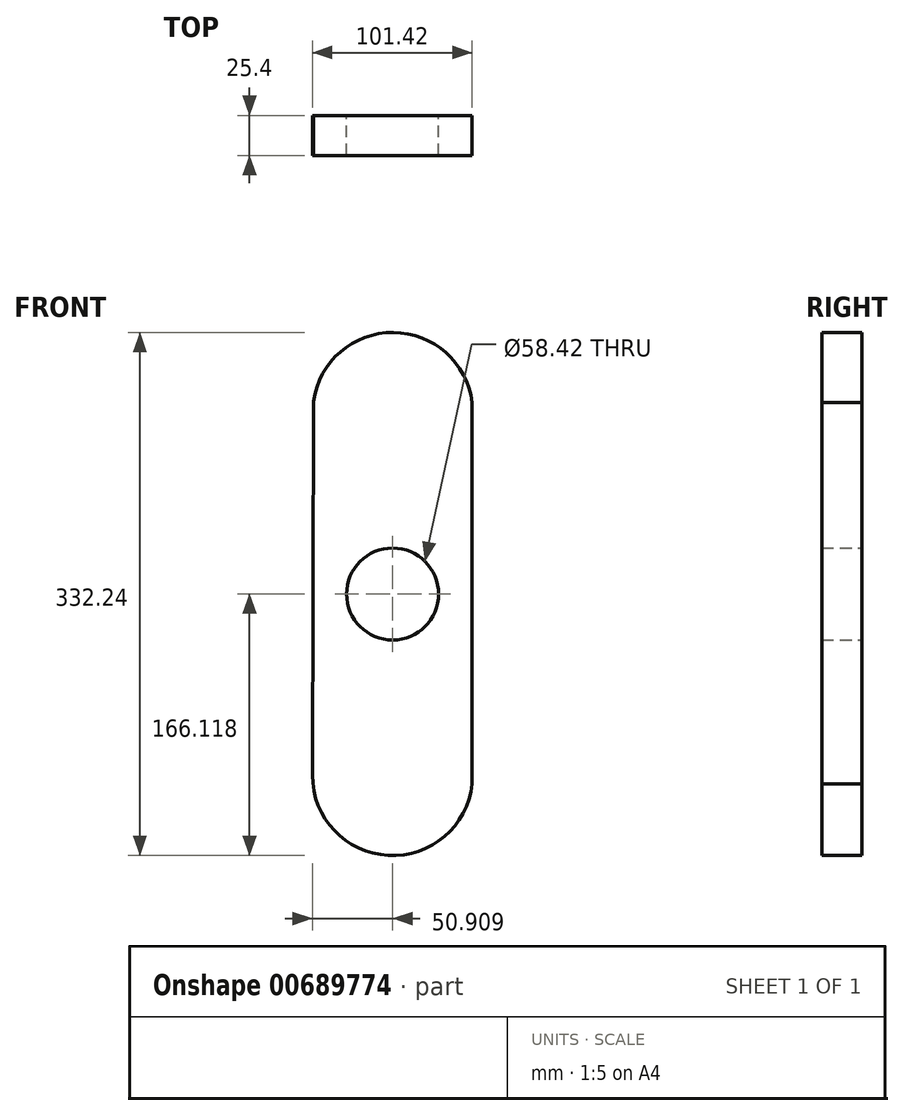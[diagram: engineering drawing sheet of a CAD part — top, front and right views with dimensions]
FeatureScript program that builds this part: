
annotation { "Feature Type Name" : "Feature", "Feature Type Description" : "" }
export const myFeature = defineFeature(function(context is Context, id is Id, definition is map)
    precondition{}
    {
        {
            var Q0;
            Q0=qCreatedBy(makeId("Front.planeOp"),FACE);
            var sketch = newSketch(context, id + "F0", { "sketchPlane" : qUnion([Q0])});
            skArc(sketch, "E0", {"start": v(50.45, 146.56) * mm, "mid": v(-0.24, 203.8) * mm, "end": v(-50.39, 146.08) * mm});
            skArc(sketch, "E1", {"start": v(-50.97, -77.45) * mm, "mid": v(2.49, -128.37) * mm, "end": v(50.45, -72.25) * mm});
            skLineSegment(sketch, "E2", {"start": v(50.45, 159.33) * mm, "end": v(50.45, -82.93) * mm});
            skLineSegment(sketch, "E3", {"start": v(-50.35, 160.07) * mm, "end": v(-50.99, -82.93) * mm});
            skLineSegment(sketch, "E4", {"start": v(0, 152.94) * mm, "end": v(-0.12, -77.59) * mm, "construction": true});
            skCircle(sketch, "E5", {"center": v(-0.06, 37.68) * mm, "radius": 29.2 * mm});
            skSolve(sketch);
        }
        {
            var Q0;
            {var subQ0=sQuery(id+"F0.wireOp",EDGE,"E2");var subQ1=sQuery(id+"F0.wireOp",EDGE,"E0");var subQ3=makeQuery(id+"F0.imprint","INTERSECT",VERTEX,{"disambiguationData":[OD(1.0)],"derivedFrom":[subQ1,subQ0]});Q0=makeQuery(id+"F0.imprint","IMPRINT",FACE,{"disambiguationData":[TD([[makeQuery(id+"F0.imprint","IMPRINT",EDGE,{"disambiguationData":[TD([[subQ3,-1.0]])],"derivedFrom":subQ1}),1.0]])]});}
            extrude(context, id + "F1", {"entities" : qUnion([Q0]), "depth" : 25.4 * mm, "offsetDistance" : 25.4 * mm});
        }
    });
